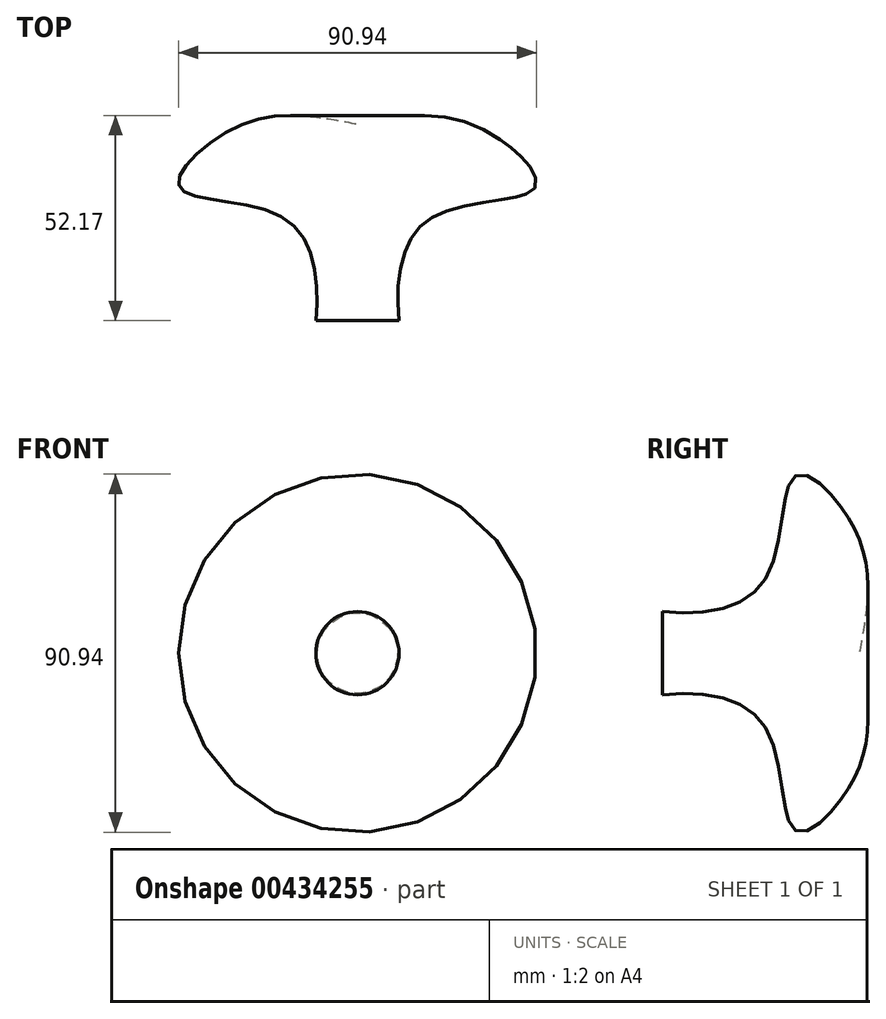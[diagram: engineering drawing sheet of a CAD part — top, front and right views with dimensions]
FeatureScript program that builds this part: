
annotation { "Feature Type Name" : "Feature", "Feature Type Description" : "" }
export const myFeature = defineFeature(function(context is Context, id is Id, definition is map)
    precondition{}
    {
        {
            var Q0;
            Q0=qCreatedBy(makeId("Top.planeOp"),FACE);
            var sketch = newSketch(context, id + "F0", { "sketchPlane" : qUnion([Q0])});
            skLineSegment(sketch, "E0", {"start": v(0, 0) * mm, "end": v(0, 50) * mm});
            skFitSpline(sketch, "E1", {"points": [v(-10.58, 0) * mm, v(-18.99, 26.26) * mm, v(-45.2, 33.99) * mm, v(-29.4, 49.79) * mm, v(0, 50) * mm], "startDerivative": vector(11.88, 115.28) * mm, "endDerivative": vector(115.91, -20.24) * mm});
            skLineSegment(sketch, "E2", {"start": v(0, 0) * mm, "end": v(-10.58, 0) * mm});
            skSolve(sketch);
        }
        {
            var Q0;
            Q0=makeQuery(id+"F0.imprint","IMPRINT",FACE,{"disambiguationData":[TD([[makeQuery(id+"F0.imprint","IMPRINT",EDGE,{"derivedFrom":sQuery(id+"F0.wireOp",EDGE,"E0")}),1.0]])]});
            var Q1;
            Q1=sQuery(id+"F0.wireOp",EDGE,"E0");
            revolve(context, id + "F1", {"entities" : qUnion([Q0]), "axis" : qUnion([Q1]), "revolveType" : RevolveType.FULL});
        }
    });
